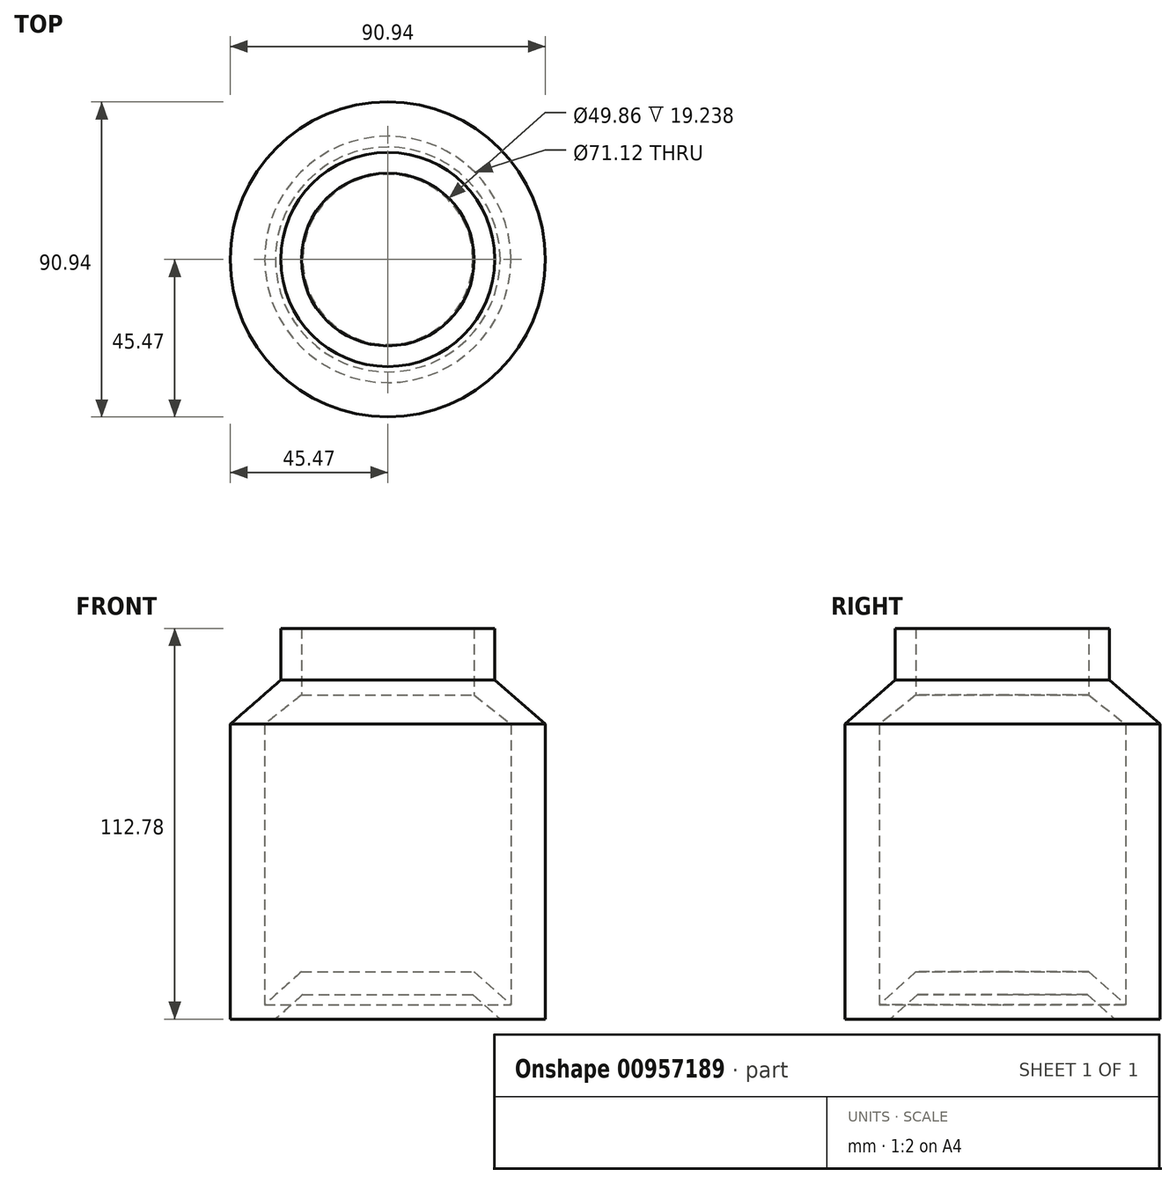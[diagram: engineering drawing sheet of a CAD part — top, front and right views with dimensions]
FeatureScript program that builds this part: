
annotation { "Feature Type Name" : "Feature", "Feature Type Description" : "" }
export const myFeature = defineFeature(function(context is Context, id is Id, definition is map)
    precondition{}
    {
        {
            var Q0;
            Q0=qCreatedBy(makeId("Front.planeOp"),FACE);
            var sketch = newSketch(context, id + "F0", { "sketchPlane" : qUnion([Q0])});
            skLineSegment(sketch, "E0", {"start": v(0, 0) * mm, "end": v(0, 88.03) * mm, "construction": true});
            skLineSegment(sketch, "E1", {"start": v(0, 0) * mm, "end": v(24.54, 0) * mm});
            skLineSegment(sketch, "E2", {"start": v(24.54, 0) * mm, "end": v(32.45, -7.1) * mm});
            skLineSegment(sketch, "E3", {"start": v(32.45, -7.1) * mm, "end": v(45.47, -7.1) * mm});
            skLineSegment(sketch, "E4", {"start": v(45.47, -7.1) * mm, "end": v(45.47, 78.03) * mm});
            skLineSegment(sketch, "E5", {"start": v(45.47, 78.03) * mm, "end": v(30.9, 90.8) * mm});
            skLineSegment(sketch, "E6", {"start": v(30.9, 90.8) * mm, "end": v(30.9, 105.69) * mm});
            skLineSegment(sketch, "E7", {"start": v(30.9, 105.69) * mm, "end": v(24.93, 105.69) * mm});
            skLineSegment(sketch, "E8", {"start": v(24.93, 105.69) * mm, "end": v(24.93, 86.45) * mm});
            skLineSegment(sketch, "E9", {"start": v(24.93, 86.45) * mm, "end": v(35.56, 78.03) * mm});
            skLineSegment(sketch, "E10", {"start": v(35.56, -2.96) * mm, "end": v(24.93, 6.58) * mm});
            skLineSegment(sketch, "E11", {"start": v(24.93, 6.58) * mm, "end": v(0, 6.58) * mm});
            skLineSegment(sketch, "E12", {"start": v(0, 6.58) * mm, "end": v(0, 0) * mm});
            skLineSegment(sketch, "E13", {"start": v(35.56, -2.96) * mm, "end": v(35.56, 78.03) * mm});
            skSolve(sketch);
        }
        {
            var Q0;
            Q0 = qSketchRegion(id + "F0", true);
            var Q1;
            Q1=sQuery(id+"F0.wireOp",EDGE,"E0");
            revolve(context, id + "F1", {"surfaceOperationType" : NewSurfaceOperationType.NEW, "entities" : qUnion([Q0]), "axis" : qUnion([Q1]), "revolveType" : RevolveType.FULL});
        }
    });
